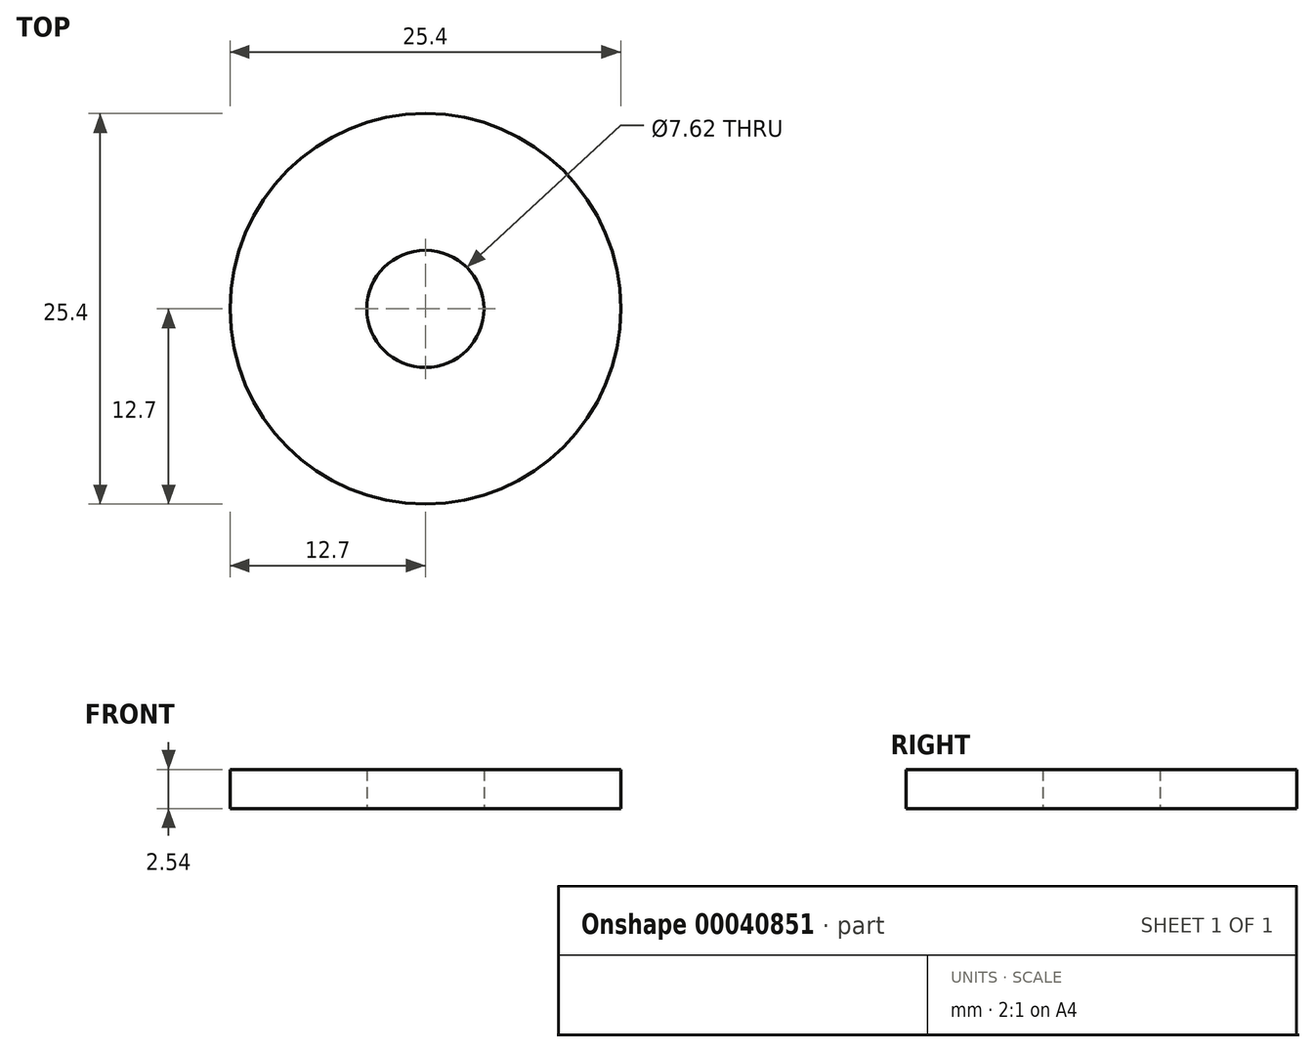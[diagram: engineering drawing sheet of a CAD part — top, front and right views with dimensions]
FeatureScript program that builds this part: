
annotation { "Feature Type Name" : "Feature", "Feature Type Description" : "" }
export const myFeature = defineFeature(function(context is Context, id is Id, definition is map)
    precondition{}
    {
        {
            var Q0;
            Q0=qCreatedBy(makeId("Top.planeOp"),FACE);
            var sketch = newSketch(context, id + "F0", { "sketchPlane" : qUnion([Q0])});
            skLineSegment(sketch, "E0", {"start": v(0, 0) * mm, "end": v(12.7, 0) * mm});
            skLineSegment(sketch, "E1", {"start": v(0, 0) * mm, "end": v(3.81, 0) * mm});
            skCircle(sketch, "E2", {"center": v(0, 0) * mm, "radius": 12.7 * mm});
            skCircle(sketch, "E3", {"center": v(0, 0) * mm, "radius": 3.81 * mm});
            skSolve(sketch);
        }
        {
            var Q0;
            Q0=makeQuery(id+"F0.imprint","IMPRINT",FACE,{"disambiguationData":[TD([[makeQuery(id+"F0.imprint","IMPRINT",EDGE,{"derivedFrom":sQuery(id+"F0.wireOp",EDGE,"E2")}),1.0]])]});
            extrude(context, id + "F1", {"entities" : qUnion([Q0]), "depth" : 2.54 * mm});
        }
    });
